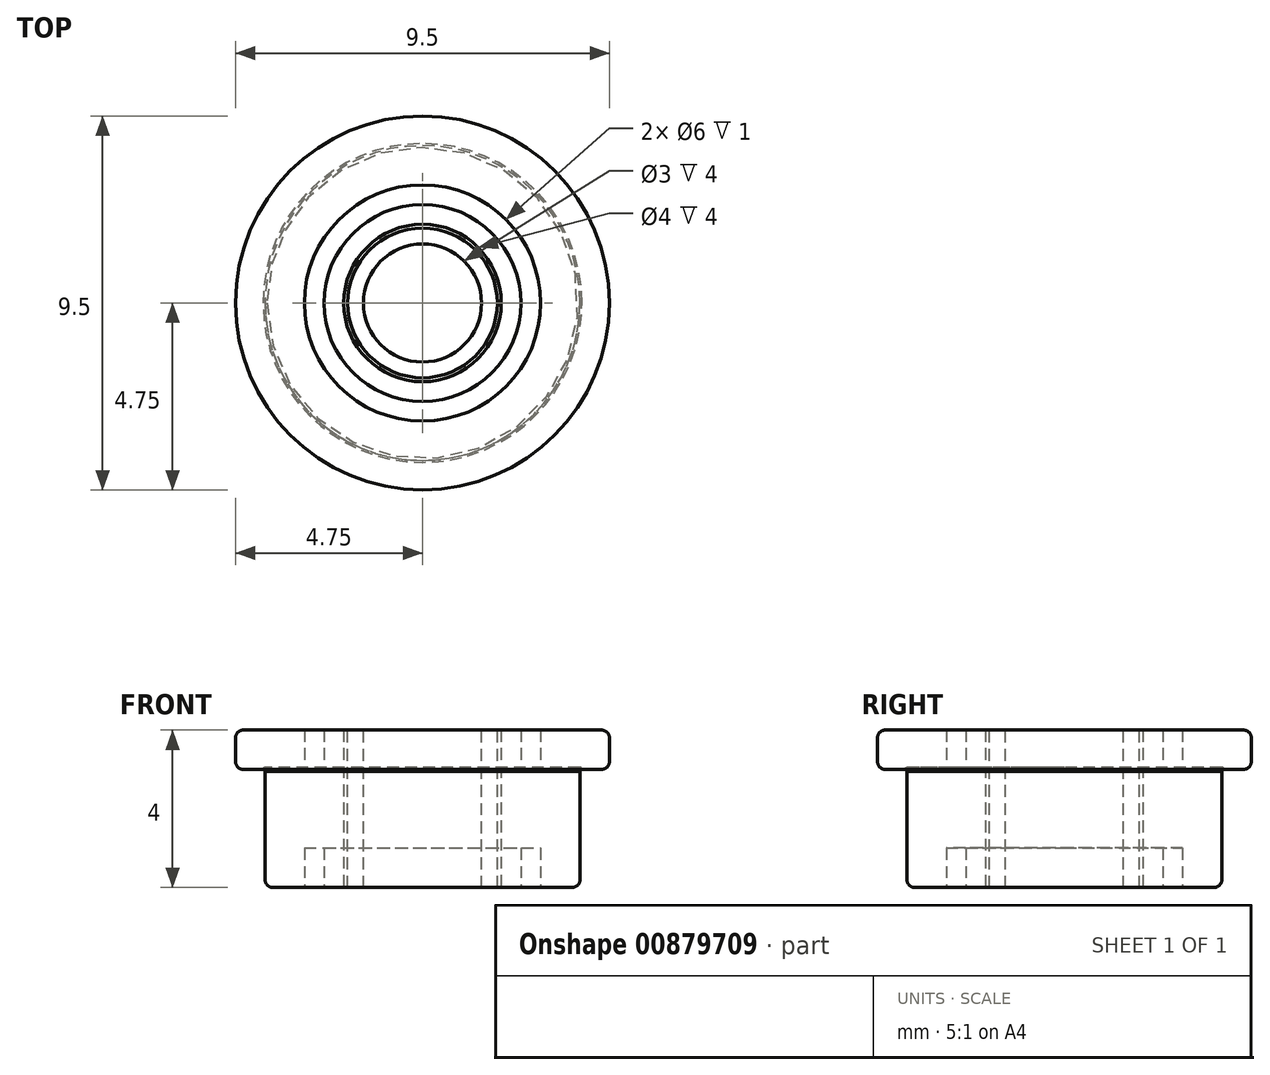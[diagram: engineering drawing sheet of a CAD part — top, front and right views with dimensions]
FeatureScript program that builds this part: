
annotation { "Feature Type Name" : "Feature", "Feature Type Description" : "" }
export const myFeature = defineFeature(function(context is Context, id is Id, definition is map)
    precondition{}
    {
        {
            var Q0;
            Q0=qCreatedBy(makeId("Front.planeOp"),FACE);
            var sketch = newSketch(context, id + "F0", { "sketchPlane" : qUnion([Q0])});
            skLineSegment(sketch, "E0", {"start": v(2, 4) * mm, "end": v(4.75, 4) * mm});
            skLineSegment(sketch, "E1", {"start": v(4.75, 4) * mm, "end": v(4.75, 3) * mm});
            skLineSegment(sketch, "E2", {"start": v(4.75, 3) * mm, "end": v(4.05, 3) * mm});
            skLineSegment(sketch, "E3", {"start": v(4, 2.95) * mm, "end": v(4, 0) * mm});
            skLineSegment(sketch, "E4", {"start": v(4, 0) * mm, "end": v(2, 0) * mm});
            skLineSegment(sketch, "E5", {"start": v(0, 0) * mm, "end": v(0, 4) * mm});
            skLineSegment(sketch, "E6", {"start": v(0, 9) * mm, "end": v(0, 4) * mm, "construction": true});
            skLineSegment(sketch, "E7", {"start": v(2, 4) * mm, "end": v(2, 0) * mm});
            skLineSegment(sketch, "E8.trimOffspring", {"start": v(0, 0) * mm, "end": v(0, -6) * mm, "construction": true});
            skLineSegment(sketch, "E9.bottom", {"start": v(2.5, 4) * mm, "end": v(3, 4) * mm});
            skLineSegment(sketch, "E9.top", {"start": v(2.5, 3) * mm, "end": v(3, 3) * mm});
            skLineSegment(sketch, "E9.left", {"start": v(2.5, 4) * mm, "end": v(2.5, 3) * mm});
            skLineSegment(sketch, "E9.right", {"start": v(3, 4) * mm, "end": v(3, 3) * mm});
            skLineSegment(sketch, "E10.bottom", {"start": v(3, 0) * mm, "end": v(2.5, 0) * mm});
            skLineSegment(sketch, "E10.top", {"start": v(3, 1) * mm, "end": v(2.5, 1) * mm});
            skLineSegment(sketch, "E10.left", {"start": v(3, 0) * mm, "end": v(3, 1) * mm});
            skLineSegment(sketch, "E10.right", {"start": v(2.5, 0) * mm, "end": v(2.5, 1) * mm});
            skArc(sketch, "E11", {"start": v(4.05, 3) * mm, "mid": v(3.96, 3.04) * mm, "end": v(4, 2.95) * mm});
            skSolve(sketch);
        }
        {
            var Q0;
            {var subQ9=sQuery(id+"F0.wireOp",EDGE,"E1");Q0=makeQuery(id+"F0.imprint","IMPRINT",FACE,{"disambiguationData":[TD([[makeQuery(id+"F0.imprint","IMPRINT",EDGE,{"derivedFrom":subQ9}),-1.0]])]});}
            var Q1;
            Q1=sQuery(id+"F0.wireOp",EDGE,"E5");
            revolve(context, id + "F1", {"surfaceOperationType" : NewSurfaceOperationType.NEW, "entities" : qUnion([Q0]), "axis" : qUnion([Q1]), "revolveType" : RevolveType.FULL});
        }
        {
            var Q0;
            {var subQ0=sQuery(id+"F0.wireOp",EDGE,"E0");Q0=makeQuery(id+"F1.opRevolve","SWEPT_FACE",FACE,{"disambiguationData":[OSD([subQ0]),TDD([makeQuery(id+"F0.imprint","IMPRINT",EDGE,{"disambiguationData":[TD([[makeQuery(id+"F0.imprint","INTERSECT",VERTEX,{"derivedFrom":[subQ0,sQuery(id+"F0.wireOp",EDGE,"E7")]}),-1.0]])],"derivedFrom":subQ0})])]});}
            var sketch = newSketch(context, id + "F2", { "sketchPlane" : qUnion([Q0])});
            skCircle(sketch, "E12", {"center": v(0, 0) * mm, "radius": 1.9 * mm});
            skCircle(sketch, "E13", {"center": v(0, 0) * mm, "radius": 1.5 * mm});
            skSolve(sketch);
        }
        {
            var Q0;
            Q0 = qSketchRegion(id + "F2", true);
            extrude(context, id + "F3", {"entities" : qUnion([Q0]), "operationType" : NewBodyOperationType.ADD, "oppositeDirection" : true, "depth" : 4 * mm, "offsetDistance" : 25 * mm});
        }
        {
            var Q0;
            Q0=makeQuery(id+"F1.opRevolve","SWEPT_EDGE",EDGE,{"disambiguationData":[OSD([sQuery(id+"F0.wireOp",EDGE,"E0"),sQuery(id+"F0.wireOp",EDGE,"E1")])]});
            var Q1;
            Q1=makeQuery(id+"F1.opRevolve","SWEPT_EDGE",EDGE,{"disambiguationData":[OSD([sQuery(id+"F0.wireOp",EDGE,"E1"),sQuery(id+"F0.wireOp",EDGE,"E2")])]});
            var Q2;
            Q2=makeQuery(id+"F1.opRevolve","SWEPT_EDGE",EDGE,{"disambiguationData":[OSD([sQuery(id+"F0.wireOp",EDGE,"E3"),sQuery(id+"F0.wireOp",EDGE,"E4")])]});
            fillet(context, id + "F4", {"entities" : qUnion([Q0, Q1, Q2]), "radius" : 0.2 * mm, "tangentPropagation" : true, "allowEdgeOverflow" : false});
        }
    });
